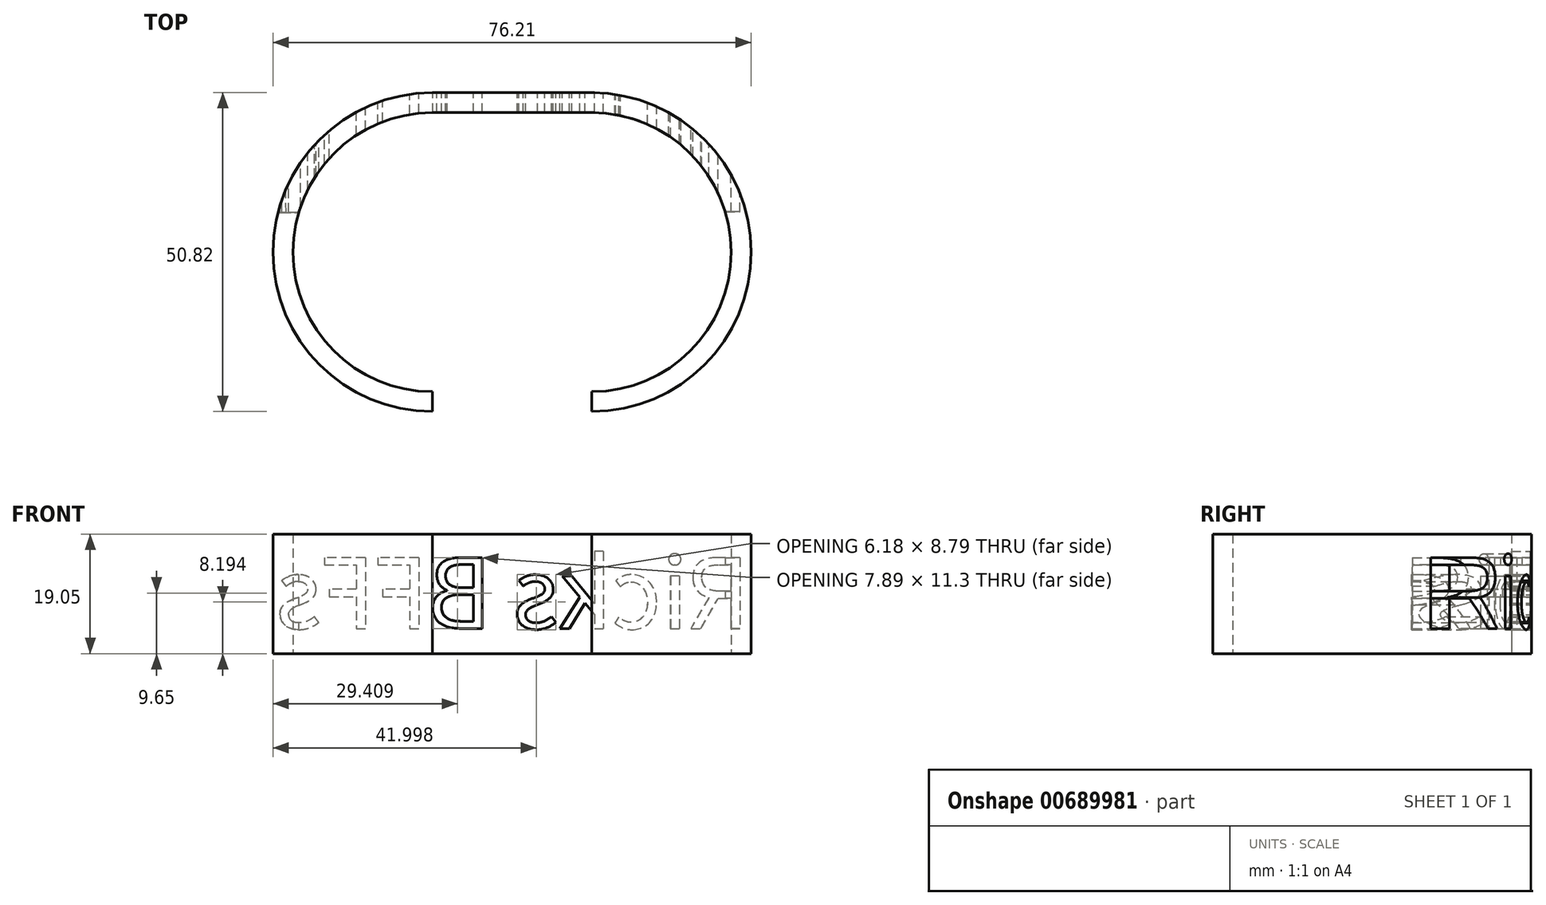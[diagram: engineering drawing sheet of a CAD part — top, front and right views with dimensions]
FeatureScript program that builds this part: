
annotation { "Feature Type Name" : "Feature", "Feature Type Description" : "" }
export const myFeature = defineFeature(function(context is Context, id is Id, definition is map)
    precondition{}
    {
        {
            var Q0;
            Q0=qCreatedBy(makeId("Top.planeOp"),FACE);
            var sketch = newSketch(context, id + "F0", { "sketchPlane" : qUnion([Q0])});
            skArc(sketch, "E0", {"start": v(-34.93, 22.23) * mm, "mid": v(-50.64, 15.72) * mm, "end": v(-57.15, 0) * mm});
            skLineSegment(sketch, "E1", {"start": v(-34.93, 22.23) * mm, "end": v(-22.23, 22.23) * mm});
            skArc(sketch, "E2.0", {"start": v(-34.93, 25.4) * mm, "mid": v(-52.89, 17.96) * mm, "end": v(-60.33, 0) * mm});
            skLineSegment(sketch, "E3", {"start": v(-22.23, 25.42) * mm, "end": v(-34.93, 25.4) * mm});
            skArc(sketch, "E4.MirrorCS", {"start": v(-9.52, 25.4) * mm, "mid": v(8.44, 17.96) * mm, "end": v(15.88, 0) * mm});
            skArc(sketch, "E5.MirrorCS", {"start": v(-9.52, 22.23) * mm, "mid": v(6.2, 15.72) * mm, "end": v(12.7, 0) * mm});
            skLineSegment(sketch, "E6.MirrorCS", {"start": v(-22.23, 25.42) * mm, "end": v(-9.52, 25.4) * mm});
            skLineSegment(sketch, "E7.MirrorCS", {"start": v(-9.52, 22.23) * mm, "end": v(-22.23, 22.23) * mm});
            skArc(sketch, "E8.MirrorCS", {"start": v(-34.93, -25.4) * mm, "mid": v(-52.89, -17.96) * mm, "end": v(-60.33, 0) * mm});
            skArc(sketch, "E9.MirrorCS", {"start": v(-34.93, -22.23) * mm, "mid": v(-50.64, -15.72) * mm, "end": v(-57.15, 0) * mm});
            skArc(sketch, "E10.MirrorCS", {"start": v(-9.52, -22.23) * mm, "mid": v(6.2, -15.72) * mm, "end": v(12.7, 0) * mm});
            skArc(sketch, "E11.MirrorCS", {"start": v(-9.52, -25.4) * mm, "mid": v(8.44, -17.96) * mm, "end": v(15.88, 0) * mm});
            skLineSegment(sketch, "E12", {"start": v(-34.93, -25.4) * mm, "end": v(-34.93, -22.23) * mm});
            skLineSegment(sketch, "E13", {"start": v(-9.52, -25.4) * mm, "end": v(-9.52, -22.23) * mm});
            skSolve(sketch);
        }
        {
            var Q0;
            Q0 = qSketchRegion(id + "F0", true);
            extrude(context, id + "F1", {"entities" : qUnion([Q0]), "depth" : 19.05 * mm, "offsetDistance" : 25.4 * mm});
        }
        {
            var Q0;
            Q0=makeQuery(id+"F1.opExtrude","SWEPT_FACE",FACE,{"disambiguationData":[OSD([sQuery(id+"F0.wireOp",EDGE,"E3")])]});
            var sketch = newSketch(context, id + "F2", { "sketchPlane" : qUnion([Q0])});
            skText(sketch, "E14", { "text": "Ricks BFFs", "fontName": "NotoSansCJKjp-Regular.otf"});
            const initialGuessF2  = {"E14": [-0.01566, 0.004, 1, 0, 0.0111]};
            skSetInitialGuess(sketch, initialGuessF2);
            skSolve(sketch);
        }
        {
            var Q0;
            Q0 = qSketchRegion(id + "F2", true);
            extrude(context, id + "F3", {"entities" : qUnion([Q0]), "operationType" : NewBodyOperationType.REMOVE, "oppositeDirection" : true, "depth" : 19.05 * mm, "hasOffset" : true, "offsetDistance" : 25.4 * mm});
        }
    });
